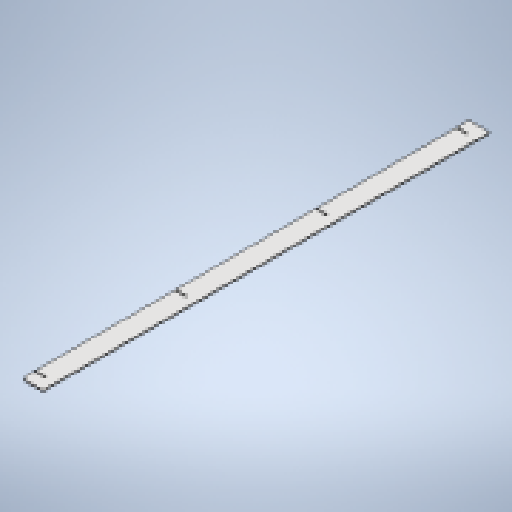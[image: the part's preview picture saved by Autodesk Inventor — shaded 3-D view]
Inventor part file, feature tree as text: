
AUTODESK INVENTOR PART (.ipt)
format: ipt  version: 2025 (Build 290162010, 162A)  size: 313,856 bytes
history: native  units: mm
features: other x3, sketch x3, sheet_metal_op x1, extrude x1, chamfer x1
ambient origin geometry x8: Origin, YZ Plane, XZ Plane, XY Plane, X Axis, Y Axis, Z Axis, Center Point
bodies: Solid1 (feature_tree)
feature tree (9):
  sheet_metal_op  "Face1"
  extrude  "Extrusion1"  Depth=1080.0mm
  chamfer  "Corner Round3"
  other  "Mark1"
  sketch  "Sketch1"  dims[d0=50.0mm d1=1080.0mm]
  other  "Plate1"
  sketch  "Sketch2"  dims[d2=3.0mm]
  sketch  "Sketch3"  dims[d15=170.0mm d16=3.0mm d17=26.0mm d18=170.0mm d19=26.0mm d20=3.0mm d21=0.0mm d22=0.0mm d23=3.0mm d24=26.0mm d25=340.0mm d26=26.0mm d27=3.0mm d28=3.0mm d29=340.0mm d30=6.0mm]
  other  "Definition1"
